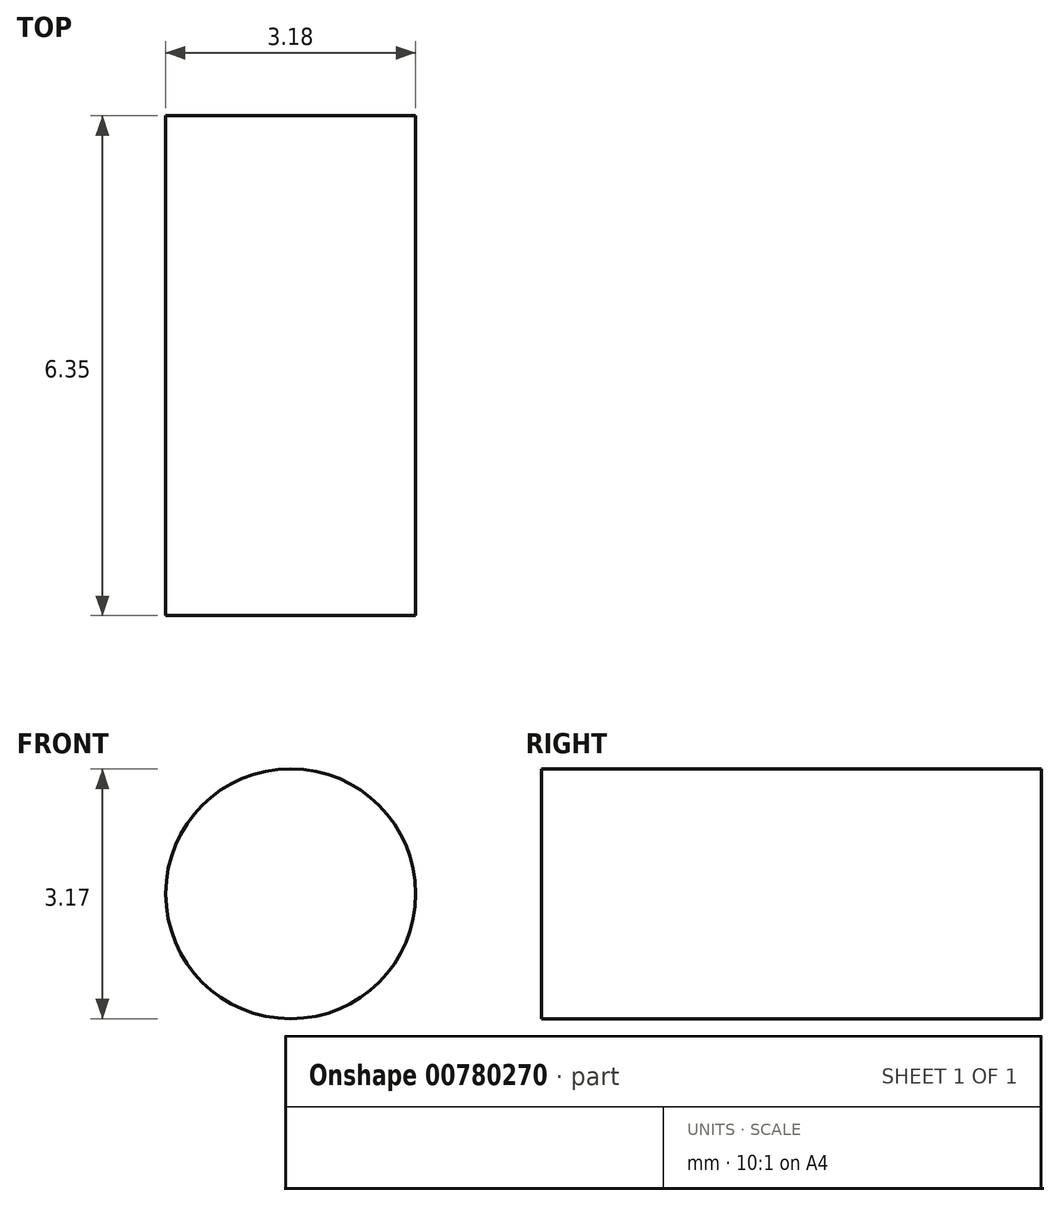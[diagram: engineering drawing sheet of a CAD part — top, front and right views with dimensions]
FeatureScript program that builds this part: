
annotation { "Feature Type Name" : "Feature", "Feature Type Description" : "" }
export const myFeature = defineFeature(function(context is Context, id is Id, definition is map)
    precondition{}
    {
        {
            var Q0;
            Q0=qCreatedBy(makeId("Front.planeOp"),FACE);
            var sketch = newSketch(context, id + "F0", { "sketchPlane" : qUnion([Q0])});
            skCircle(sketch, "E0", {"center": v(-212.06, -66.61) * mm, "radius": 1.59 * mm});
            skSolve(sketch);
        }
        {
            var Q0;
            Q0 = qSketchRegion(id + "F0", true);
            extrude(context, id + "F1", {"entities" : qUnion([Q0]), "depth" : 6.35 * mm, "offsetDistance" : 25 * mm});
        }
    });
